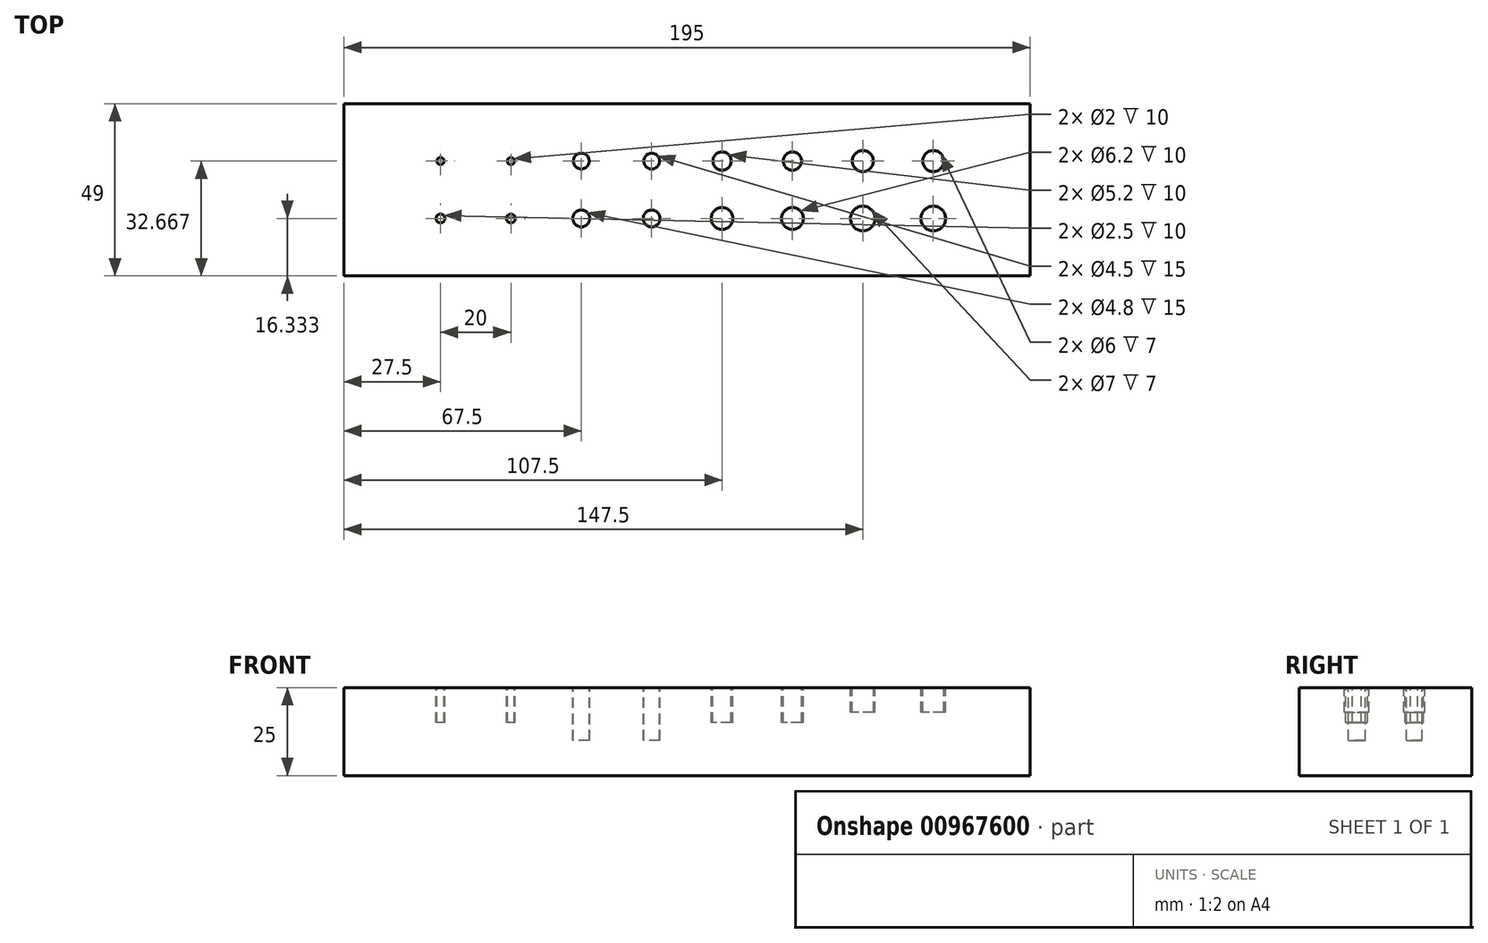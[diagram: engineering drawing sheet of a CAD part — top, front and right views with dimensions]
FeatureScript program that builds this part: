
annotation { "Feature Type Name" : "Feature", "Feature Type Description" : "" }
export const myFeature = defineFeature(function(context is Context, id is Id, definition is map)
    precondition{}
    {
        {
            var Q0;
            Q0=qCreatedBy(makeId("Top.planeOp"),FACE);
            var sketch = newSketch(context, id + "F0", { "sketchPlane" : qUnion([Q0])});
            skLineSegment(sketch, "E0.bottom", {"start": v(0, 0) * mm, "end": v(195, 0) * mm});
            skLineSegment(sketch, "E0.top", {"start": v(0, 49) * mm, "end": v(195, 49) * mm});
            skLineSegment(sketch, "E0.left", {"start": v(0, 0) * mm, "end": v(0, 49) * mm});
            skLineSegment(sketch, "E0.right", {"start": v(195, 0) * mm, "end": v(195, 49) * mm});
            skLineSegment(sketch, "E1", {"start": v(0, 24.5) * mm, "end": v(195, 24.5) * mm, "construction": true});
            skLineSegment(sketch, "E2", {"start": v(97.5, 49) * mm, "end": v(97.5, 0) * mm, "construction": true});
            skLineSegment(sketch, "E3", {"start": v(0, 16.33) * mm, "end": v(195, 16.33) * mm, "construction": true});
            skCircle(sketch, "E4", {"center": v(27.5, 32.67) * mm, "radius": 1 * mm});
            skCircle(sketch, "E5", {"center": v(47.5, 32.67) * mm, "radius": 1 * mm});
            skCircle(sketch, "E6", {"center": v(67.5, 32.67) * mm, "radius": 2.25 * mm});
            skCircle(sketch, "E7", {"center": v(87.5, 32.67) * mm, "radius": 2.25 * mm});
            skCircle(sketch, "E8", {"center": v(107.5, 32.67) * mm, "radius": 2.6 * mm});
            skCircle(sketch, "E9", {"center": v(127.5, 32.67) * mm, "radius": 2.6 * mm});
            skCircle(sketch, "E10", {"center": v(147.5, 32.67) * mm, "radius": 3 * mm});
            skCircle(sketch, "E11", {"center": v(167.5, 32.67) * mm, "radius": 3 * mm});
            skCircle(sketch, "E12", {"center": v(27.5, 16.33) * mm, "radius": 1.25 * mm});
            skCircle(sketch, "E13", {"center": v(47.5, 16.33) * mm, "radius": 1.25 * mm});
            skCircle(sketch, "E14", {"center": v(67.5, 16.33) * mm, "radius": 2.4 * mm});
            skCircle(sketch, "E15", {"center": v(87.5, 16.33) * mm, "radius": 2.4 * mm});
            skCircle(sketch, "E16", {"center": v(107.5, 16.33) * mm, "radius": 3.1 * mm});
            skCircle(sketch, "E17", {"center": v(127.5, 16.33) * mm, "radius": 3.1 * mm});
            skCircle(sketch, "E18", {"center": v(147.5, 16.33) * mm, "radius": 3.5 * mm});
            skCircle(sketch, "E19", {"center": v(167.5, 16.33) * mm, "radius": 3.5 * mm});
            skLineSegment(sketch, "E20", {"start": v(0, 32.67) * mm, "end": v(195, 32.67) * mm, "construction": true});
            skSolve(sketch);
        }
        {
            var Q0;
            Q0=makeQuery(id+"F0.imprint","IMPRINT",FACE,{"disambiguationData":[TD([[makeQuery(id+"F0.imprint","IMPRINT",EDGE,{"derivedFrom":sQuery(id+"F0.wireOp",EDGE,"E0.bottom")}),1.0]])]});
            var Q1;
            Q1=makeQuery(id+"F0.imprint","IMPRINT",FACE,{"disambiguationData":[TD([[makeQuery(id+"F0.imprint","IMPRINT",EDGE,{"derivedFrom":sQuery(id+"F0.wireOp",EDGE,"E4")}),1.0]])]});
            var Q2;
            Q2=makeQuery(id+"F0.imprint","IMPRINT",FACE,{"disambiguationData":[TD([[makeQuery(id+"F0.imprint","IMPRINT",EDGE,{"derivedFrom":sQuery(id+"F0.wireOp",EDGE,"E12")}),1.0]])]});
            var Q3;
            Q3=makeQuery(id+"F0.imprint","IMPRINT",FACE,{"disambiguationData":[TD([[makeQuery(id+"F0.imprint","IMPRINT",EDGE,{"derivedFrom":sQuery(id+"F0.wireOp",EDGE,"E13")}),1.0]])]});
            var Q4;
            Q4=makeQuery(id+"F0.imprint","IMPRINT",FACE,{"disambiguationData":[TD([[makeQuery(id+"F0.imprint","IMPRINT",EDGE,{"derivedFrom":sQuery(id+"F0.wireOp",EDGE,"E5")}),1.0]])]});
            var Q5;
            Q5=makeQuery(id+"F0.imprint","IMPRINT",FACE,{"disambiguationData":[TD([[makeQuery(id+"F0.imprint","IMPRINT",EDGE,{"derivedFrom":sQuery(id+"F0.wireOp",EDGE,"E6")}),1.0]])]});
            var Q6;
            Q6=makeQuery(id+"F0.imprint","IMPRINT",FACE,{"disambiguationData":[TD([[makeQuery(id+"F0.imprint","IMPRINT",EDGE,{"derivedFrom":sQuery(id+"F0.wireOp",EDGE,"E14")}),1.0]])]});
            var Q7;
            Q7=makeQuery(id+"F0.imprint","IMPRINT",FACE,{"disambiguationData":[TD([[makeQuery(id+"F0.imprint","IMPRINT",EDGE,{"derivedFrom":sQuery(id+"F0.wireOp",EDGE,"E7")}),1.0]])]});
            var Q8;
            Q8=makeQuery(id+"F0.imprint","IMPRINT",FACE,{"disambiguationData":[TD([[makeQuery(id+"F0.imprint","IMPRINT",EDGE,{"derivedFrom":sQuery(id+"F0.wireOp",EDGE,"E15")}),1.0]])]});
            var Q9;
            Q9=makeQuery(id+"F0.imprint","IMPRINT",FACE,{"disambiguationData":[TD([[makeQuery(id+"F0.imprint","IMPRINT",EDGE,{"derivedFrom":sQuery(id+"F0.wireOp",EDGE,"E16")}),1.0]])]});
            var Q10;
            Q10=makeQuery(id+"F0.imprint","IMPRINT",FACE,{"disambiguationData":[TD([[makeQuery(id+"F0.imprint","IMPRINT",EDGE,{"derivedFrom":sQuery(id+"F0.wireOp",EDGE,"E8")}),1.0]])]});
            var Q11;
            Q11=makeQuery(id+"F0.imprint","IMPRINT",FACE,{"disambiguationData":[TD([[makeQuery(id+"F0.imprint","IMPRINT",EDGE,{"derivedFrom":sQuery(id+"F0.wireOp",EDGE,"E10")}),1.0]])]});
            var Q12;
            Q12=makeQuery(id+"F0.imprint","IMPRINT",FACE,{"disambiguationData":[TD([[makeQuery(id+"F0.imprint","IMPRINT",EDGE,{"derivedFrom":sQuery(id+"F0.wireOp",EDGE,"E9")}),1.0]])]});
            var Q13;
            Q13=makeQuery(id+"F0.imprint","IMPRINT",FACE,{"disambiguationData":[TD([[makeQuery(id+"F0.imprint","IMPRINT",EDGE,{"derivedFrom":sQuery(id+"F0.wireOp",EDGE,"E17")}),1.0]])]});
            var Q14;
            Q14=makeQuery(id+"F0.imprint","IMPRINT",FACE,{"disambiguationData":[TD([[makeQuery(id+"F0.imprint","IMPRINT",EDGE,{"derivedFrom":sQuery(id+"F0.wireOp",EDGE,"E18")}),1.0]])]});
            var Q15;
            Q15=makeQuery(id+"F0.imprint","IMPRINT",FACE,{"disambiguationData":[TD([[makeQuery(id+"F0.imprint","IMPRINT",EDGE,{"derivedFrom":sQuery(id+"F0.wireOp",EDGE,"E11")}),1.0]])]});
            var Q16;
            Q16=makeQuery(id+"F0.imprint","IMPRINT",FACE,{"disambiguationData":[TD([[makeQuery(id+"F0.imprint","IMPRINT",EDGE,{"derivedFrom":sQuery(id+"F0.wireOp",EDGE,"E19")}),1.0]])]});
            extrude(context, id + "F1", {"entities" : qUnion([Q0, Q1, Q2, Q3, Q4, Q5, Q6, Q7, Q8, Q9, Q10, Q11, Q12, Q13, Q14, Q15, Q16]), "oppositeDirection" : true, "depth" : 25 * mm, "offsetDistance" : 25 * mm});
        }
        {
            var Q0;
            Q0=makeQuery(id+"F0.imprint","IMPRINT",FACE,{"disambiguationData":[TD([[makeQuery(id+"F0.imprint","IMPRINT",EDGE,{"derivedFrom":sQuery(id+"F0.wireOp",EDGE,"E4")}),1.0]])]});
            var Q1;
            Q1=makeQuery(id+"F0.imprint","IMPRINT",FACE,{"disambiguationData":[TD([[makeQuery(id+"F0.imprint","IMPRINT",EDGE,{"derivedFrom":sQuery(id+"F0.wireOp",EDGE,"E5")}),1.0]])]});
            var Q2;
            Q2=makeQuery(id+"F0.imprint","IMPRINT",FACE,{"disambiguationData":[TD([[makeQuery(id+"F0.imprint","IMPRINT",EDGE,{"derivedFrom":sQuery(id+"F0.wireOp",EDGE,"E12")}),1.0]])]});
            var Q3;
            Q3=makeQuery(id+"F0.imprint","IMPRINT",FACE,{"disambiguationData":[TD([[makeQuery(id+"F0.imprint","IMPRINT",EDGE,{"derivedFrom":sQuery(id+"F0.wireOp",EDGE,"E13")}),1.0]])]});
            var Q4;
            Q4=makeQuery(id+"F0.imprint","IMPRINT",FACE,{"disambiguationData":[TD([[makeQuery(id+"F0.imprint","IMPRINT",EDGE,{"derivedFrom":sQuery(id+"F0.wireOp",EDGE,"E8")}),1.0]])]});
            var Q5;
            Q5=makeQuery(id+"F0.imprint","IMPRINT",FACE,{"disambiguationData":[TD([[makeQuery(id+"F0.imprint","IMPRINT",EDGE,{"derivedFrom":sQuery(id+"F0.wireOp",EDGE,"E16")}),1.0]])]});
            var Q6;
            Q6=makeQuery(id+"F0.imprint","IMPRINT",FACE,{"disambiguationData":[TD([[makeQuery(id+"F0.imprint","IMPRINT",EDGE,{"derivedFrom":sQuery(id+"F0.wireOp",EDGE,"E9")}),1.0]])]});
            var Q7;
            Q7=makeQuery(id+"F0.imprint","IMPRINT",FACE,{"disambiguationData":[TD([[makeQuery(id+"F0.imprint","IMPRINT",EDGE,{"derivedFrom":sQuery(id+"F0.wireOp",EDGE,"E17")}),1.0]])]});
            extrude(context, id + "F2", {"entities" : qUnion([Q0, Q1, Q2, Q3, Q4, Q5, Q6, Q7]), "operationType" : NewBodyOperationType.REMOVE, "oppositeDirection" : true, "depth" : 10 * mm, "offsetDistance" : 25 * mm});
        }
        {
            var Q0;
            Q0=makeQuery(id+"F0.imprint","IMPRINT",FACE,{"disambiguationData":[TD([[makeQuery(id+"F0.imprint","IMPRINT",EDGE,{"derivedFrom":sQuery(id+"F0.wireOp",EDGE,"E6")}),1.0]])]});
            var Q1;
            Q1=makeQuery(id+"F0.imprint","IMPRINT",FACE,{"disambiguationData":[TD([[makeQuery(id+"F0.imprint","IMPRINT",EDGE,{"derivedFrom":sQuery(id+"F0.wireOp",EDGE,"E7")}),1.0]])]});
            var Q2;
            Q2=makeQuery(id+"F0.imprint","IMPRINT",FACE,{"disambiguationData":[TD([[makeQuery(id+"F0.imprint","IMPRINT",EDGE,{"derivedFrom":sQuery(id+"F0.wireOp",EDGE,"E15")}),1.0]])]});
            var Q3;
            Q3=makeQuery(id+"F0.imprint","IMPRINT",FACE,{"disambiguationData":[TD([[makeQuery(id+"F0.imprint","IMPRINT",EDGE,{"derivedFrom":sQuery(id+"F0.wireOp",EDGE,"E14")}),1.0]])]});
            extrude(context, id + "F3", {"entities" : qUnion([Q0, Q1, Q2, Q3]), "operationType" : NewBodyOperationType.REMOVE, "oppositeDirection" : true, "depth" : 15 * mm, "offsetDistance" : 25 * mm});
        }
        {
            var Q0;
            Q0=makeQuery(id+"F0.imprint","IMPRINT",FACE,{"disambiguationData":[TD([[makeQuery(id+"F0.imprint","IMPRINT",EDGE,{"derivedFrom":sQuery(id+"F0.wireOp",EDGE,"E10")}),1.0]])]});
            var Q1;
            Q1=makeQuery(id+"F0.imprint","IMPRINT",FACE,{"disambiguationData":[TD([[makeQuery(id+"F0.imprint","IMPRINT",EDGE,{"derivedFrom":sQuery(id+"F0.wireOp",EDGE,"E18")}),1.0]])]});
            var Q2;
            Q2=makeQuery(id+"F0.imprint","IMPRINT",FACE,{"disambiguationData":[TD([[makeQuery(id+"F0.imprint","IMPRINT",EDGE,{"derivedFrom":sQuery(id+"F0.wireOp",EDGE,"E19")}),1.0]])]});
            var Q3;
            Q3=makeQuery(id+"F0.imprint","IMPRINT",FACE,{"disambiguationData":[TD([[makeQuery(id+"F0.imprint","IMPRINT",EDGE,{"derivedFrom":sQuery(id+"F0.wireOp",EDGE,"E11")}),1.0]])]});
            extrude(context, id + "F4", {"entities" : qUnion([Q0, Q1, Q2, Q3]), "operationType" : NewBodyOperationType.REMOVE, "oppositeDirection" : true, "depth" : 7 * mm, "offsetDistance" : 25 * mm});
        }
    });
